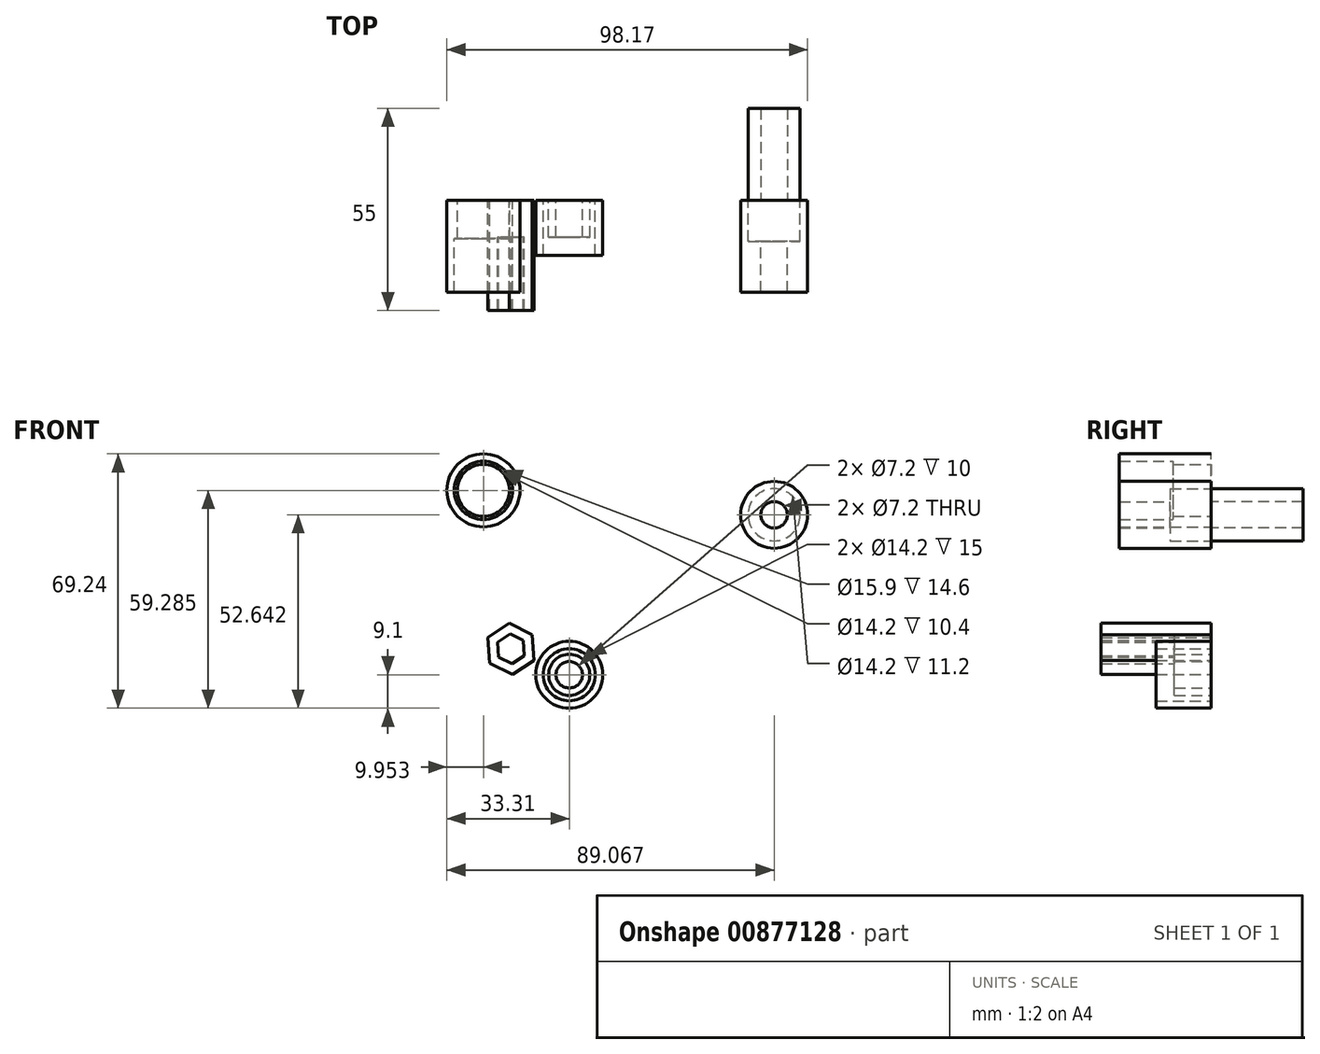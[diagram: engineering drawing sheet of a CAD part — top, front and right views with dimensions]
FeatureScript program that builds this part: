
annotation { "Feature Type Name" : "Feature", "Feature Type Description" : "" }
export const myFeature = defineFeature(function(context is Context, id is Id, definition is map)
    precondition{}
    {
        {
            var Q0;
            Q0=qCreatedBy(makeId("Front.planeOp"),FACE);
            var sketch = newSketch(context, id + "F0", { "sketchPlane" : qUnion([Q0])});
            skCircle(sketch, "E0.cCircle", {"center": v(-15.87, 7.05) * mm, "radius": 3.55 * mm, "construction": true});
            skLineSegment(sketch, "E0.0", {"start": v(-12.2, 5.23) * mm, "end": v(-15.62, 2.96) * mm});
            skLineSegment(sketch, "E0.1", {"start": v(-15.62, 2.96) * mm, "end": v(-19.3, 4.8) * mm});
            skLineSegment(sketch, "E0.2", {"start": v(-19.3, 4.8) * mm, "end": v(-19.54, 8.88) * mm});
            skLineSegment(sketch, "E0.3", {"start": v(-19.54, 8.88) * mm, "end": v(-16.12, 11.15) * mm});
            skLineSegment(sketch, "E0.4", {"start": v(-16.12, 11.15) * mm, "end": v(-12.46, 9.32) * mm});
            skLineSegment(sketch, "E0.5", {"start": v(-12.46, 9.32) * mm, "end": v(-12.2, 5.23) * mm});
            skPoint(sketch, "E0.0.midPoint", {"position": v(-13.91, 4.1) * mm});
            skLineSegment(sketch, "E1.0", {"start": v(-21.7, 3.2) * mm, "end": v(-22.13, 10.17) * mm});
            skLineSegment(sketch, "E1.1", {"start": v(-16.3, 14.03) * mm, "end": v(-10.05, 10.91) * mm});
            skLineSegment(sketch, "E1.2", {"start": v(-10.05, 10.91) * mm, "end": v(-9.62, 3.94) * mm});
            skLineSegment(sketch, "E1.3", {"start": v(-22.13, 10.17) * mm, "end": v(-16.3, 14.03) * mm});
            skLineSegment(sketch, "E1.4", {"start": v(-9.62, 3.94) * mm, "end": v(-15.45, 0.08) * mm});
            skLineSegment(sketch, "E1.5", {"start": v(-15.45, 0.08) * mm, "end": v(-21.7, 3.2) * mm});
            skSolve(sketch);
        }
        {
            var Q0;
            Q0=makeQuery(id+"F0.imprint","IMPRINT",FACE,{"disambiguationData":[TD([[makeQuery(id+"F0.imprint","IMPRINT",EDGE,{"derivedFrom":sQuery(id+"F0.wireOp",EDGE,"E0.0")}),1.0]])]});
            extrude(context, id + "F1", {"entities" : qUnion([Q0]), "depth" : 30 * mm, "offsetDistance" : 25 * mm});
        }
        {
            var Q0;
            Q0=makeQuery(id+"F0.imprint","IMPRINT",FACE,{"disambiguationData":[TD([[makeQuery(id+"F0.imprint","IMPRINT",EDGE,{"derivedFrom":sQuery(id+"F0.wireOp",EDGE,"E0.0")}),-1.0]])]});
            extrude(context, id + "F2", {"entities" : qUnion([Q0]), "operationType" : NewBodyOperationType.ADD, "depth" : 10 * mm, "offsetDistance" : 25 * mm});
        }
        {
            var Q0;
            Q0=qCreatedBy(makeId("Front.planeOp"),FACE);
            var sketch = newSketch(context, id + "F3", { "sketchPlane" : qUnion([Q0])});
            skCircle(sketch, "E2", {"center": v(0, 0) * mm, "radius": 3.6 * mm});
            skCircle(sketch, "E3.0", {"center": v(0, 0) * mm, "radius": 5.6 * mm});
            skSolve(sketch);
        }
        {
            var Q0;
            Q0 = qSketchRegion(id + "F3", true);
            extrude(context, id + "F4", {"entities" : qUnion([Q0]), "depth" : 10 * mm, "offsetDistance" : 25 * mm});
        }
        {
            var Q0;
            Q0=qCreatedBy(makeId("Front.planeOp"),FACE);
            var sketch = newSketch(context, id + "F5", { "sketchPlane" : qUnion([Q0])});
            skCircle(sketch, "E4", {"center": v(0, 0) * mm, "radius": 7.1 * mm});
            skCircle(sketch, "E5.0", {"center": v(0, 0) * mm, "radius": 9.1 * mm});
            skSolve(sketch);
        }
        {
            var Q0;
            Q0 = qSketchRegion(id + "F5", true);
            extrude(context, id + "F6", {"entities" : qUnion([Q0]), "depth" : 15 * mm, "offsetDistance" : 25 * mm});
        }
        {
            var Q0;
            Q0=qCreatedBy(makeId("Front.planeOp"),FACE);
            var sketch = newSketch(context, id + "F7", { "sketchPlane" : qUnion([Q0])});
            skCircle(sketch, "E6", {"center": v(55.76, 43.54) * mm, "radius": 3.6 * mm});
            skCircle(sketch, "E7", {"center": v(55.76, 43.54) * mm, "radius": 7.1 * mm});
            skCircle(sketch, "E8.0", {"center": v(55.76, 43.54) * mm, "radius": 9.1 * mm});
            skSolve(sketch);
        }
        {
            var Q0;
            Q0=makeQuery(id+"F7.imprint","IMPRINT",FACE,{"disambiguationData":[TD([[makeQuery(id+"F7.imprint","IMPRINT",EDGE,{"derivedFrom":sQuery(id+"F7.wireOp",EDGE,"E7")}),-1.0]])]});
            var Q1;
            Q1=makeQuery(id+"F7.imprint","IMPRINT",FACE,{"disambiguationData":[TD([[makeQuery(id+"F7.imprint","IMPRINT",EDGE,{"derivedFrom":sQuery(id+"F7.wireOp",EDGE,"E6")}),-1.0]])]});
            extrude(context, id + "F8", {"entities" : qUnion([Q0, Q1]), "depth" : 25 * mm, "offsetDistance" : 25 * mm});
        }
        {
            var Q0;
            Q0=makeQuery(id+"F8.opExtrude","CAP_FACE",FACE,{"disambiguationData":[OSD([sQuery(id+"F7.wireOp",EDGE,"E6"),sQuery(id+"F7.wireOp",EDGE,"E8.0")])],"isStart":true});
            var sketch = newSketch(context, id + "F9", { "sketchPlane" : qUnion([Q0])});
            skCircle(sketch, "E9", {"center": v(-55.76, 43.54) * mm, "radius": 7.1 * mm});
            skCircle(sketch, "E10", {"center": v(-55.76, 43.54) * mm, "radius": 3.6 * mm});
            skSolve(sketch);
        }
        {
            var Q0;
            Q0=makeQuery(id+"F9.imprint","IMPRINT",FACE,{"disambiguationData":[TD([[makeQuery(id+"F9.imprint","IMPRINT",EDGE,{"derivedFrom":sQuery(id+"F9.wireOp",EDGE,"E9")}),1.0]])]});
            extrude(context, id + "F10", {"entities" : qUnion([Q0]), "operationType" : NewBodyOperationType.REMOVE, "oppositeDirection" : true, "depth" : 11.2 * mm, "offsetDistance" : 25 * mm});
        }
        {
            var Q0;
            Q0=qCreatedBy(makeId("Front.planeOp"),FACE);
            var sketch = newSketch(context, id + "F11", { "sketchPlane" : qUnion([Q0])});
            skCircle(sketch, "E11", {"center": v(-23.36, 50.19) * mm, "radius": 7.95 * mm});
            skCircle(sketch, "E12.0", {"center": v(-23.36, 50.19) * mm, "radius": 9.95 * mm});
            skSolve(sketch);
        }
        {
            var Q0;
            Q0=makeQuery(id+"F11.imprint","IMPRINT",FACE,{"disambiguationData":[TD([[makeQuery(id+"F11.imprint","IMPRINT",EDGE,{"derivedFrom":sQuery(id+"F11.wireOp",EDGE,"E11")}),-1.0]])]});
            extrude(context, id + "F12", {"entities" : qUnion([Q0]), "depth" : 25 * mm, "offsetDistance" : 25 * mm});
        }
        {
            var Q0;
            Q0=makeQuery(id+"F12.opExtrude","CAP_FACE",FACE,{"disambiguationData":[OSD([sQuery(id+"F11.wireOp",EDGE,"E11"),sQuery(id+"F11.wireOp",EDGE,"E12.0")])],"isStart":true});
            var sketch = newSketch(context, id + "F13", { "sketchPlane" : qUnion([Q0])});
            skCircle(sketch, "E13", {"center": v(23.36, 50.19) * mm, "radius": 7.1 * mm});
            skCircle(sketch, "E14.0", {"center": v(23.36, 50.19) * mm, "radius": 8 * mm});
            skSolve(sketch);
        }
        {
            var Q0;
            Q0 = qSketchRegion(id + "F13", true);
            extrude(context, id + "F14", {"entities" : qUnion([Q0]), "operationType" : NewBodyOperationType.ADD, "oppositeDirection" : true, "depth" : 10.4 * mm, "offsetDistance" : 25 * mm});
        }
        {
            var Q0;
            Q0 = qSketchRegion(id + "F7", true);
            var Q1;
            Q1=makeQuery(id+"F7.imprint","IMPRINT",FACE,{"disambiguationData":[TD([[makeQuery(id+"F7.imprint","IMPRINT",EDGE,{"derivedFrom":sQuery(id+"F7.wireOp",EDGE,"E6")}),-1.0]])]});
            extrude(context, id + "F15", {"entities" : qUnion([Q0, Q1]), "operationType" : NewBodyOperationType.REMOVE, "oppositeDirection" : true, "depth" : 25 * mm, "offsetDistance" : 25 * mm});
        }
        {
            var Q0;
            Q0=makeQuery(id+"F7.imprint","IMPRINT",FACE,{"disambiguationData":[TD([[makeQuery(id+"F7.imprint","IMPRINT",EDGE,{"derivedFrom":sQuery(id+"F7.wireOp",EDGE,"E6")}),-1.0]])]});
            extrude(context, id + "F16", {"entities" : qUnion([Q0]), "operationType" : NewBodyOperationType.ADD, "oppositeDirection" : true, "depth" : 25 * mm, "offsetDistance" : 25 * mm});
        }
    });
